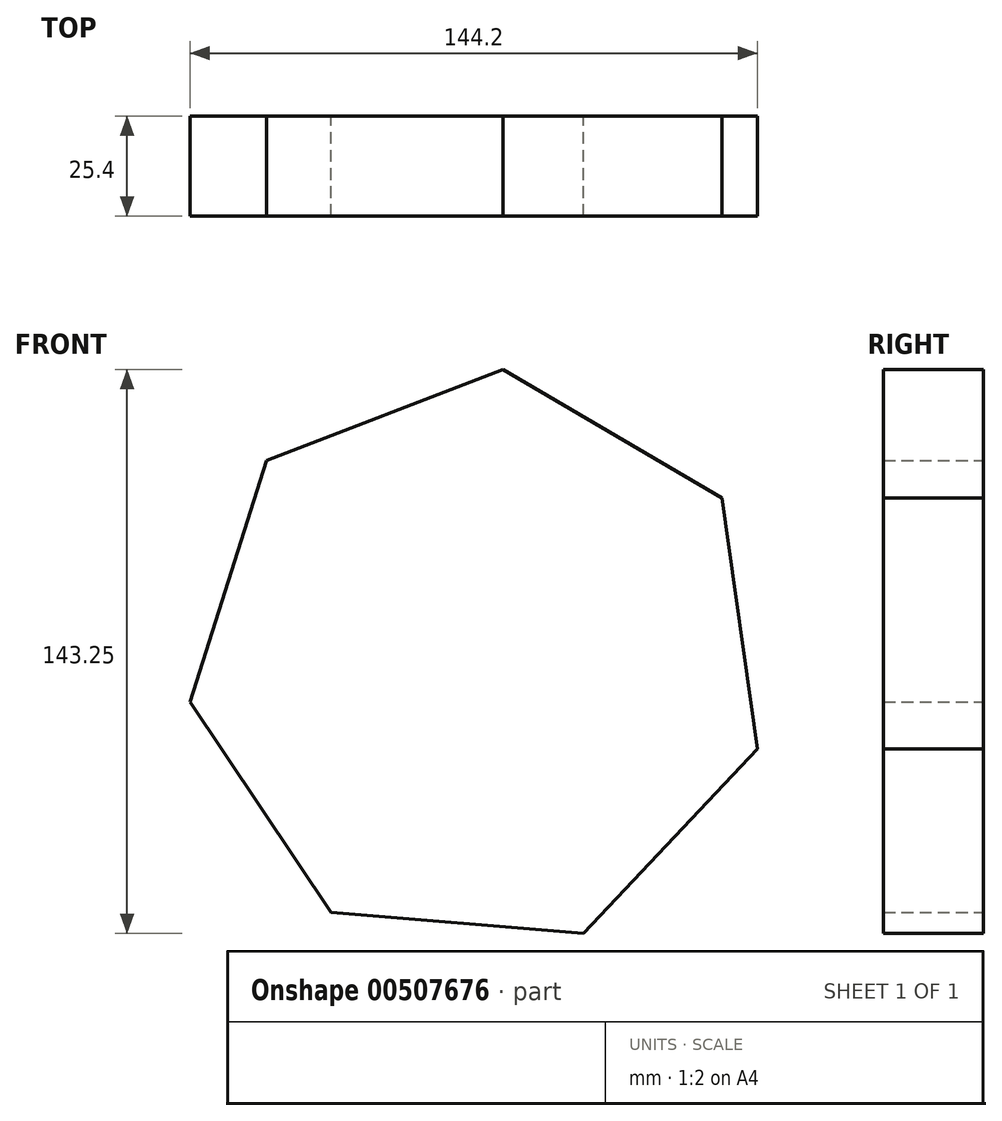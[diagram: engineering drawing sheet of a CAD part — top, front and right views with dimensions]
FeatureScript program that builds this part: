
annotation { "Feature Type Name" : "Feature", "Feature Type Description" : "" }
export const myFeature = defineFeature(function(context is Context, id is Id, definition is map)
    precondition{}
    {
        {
            var Q0;
            Q0=qCreatedBy(makeId("Front.planeOp"),FACE);
            var sketch = newSketch(context, id + "F0", { "sketchPlane" : qUnion([Q0])});
            skCircle(sketch, "E0.cCircle", {"center": v(0, 0) * mm, "radius": 74.2 * mm, "construction": true});
            skLineSegment(sketch, "E0.0", {"start": v(-37.6, -63.98) * mm, "end": v(-73.46, -10.5) * mm});
            skLineSegment(sketch, "E0.1", {"start": v(-73.46, -10.5) * mm, "end": v(-54, 50.9) * mm});
            skLineSegment(sketch, "E0.2", {"start": v(-54, 50.9) * mm, "end": v(6.12, 73.96) * mm});
            skLineSegment(sketch, "E0.3", {"start": v(6.12, 73.96) * mm, "end": v(61.64, 41.33) * mm});
            skLineSegment(sketch, "E0.4", {"start": v(61.64, 41.33) * mm, "end": v(70.74, -22.42) * mm});
            skLineSegment(sketch, "E0.5", {"start": v(70.74, -22.42) * mm, "end": v(26.58, -69.29) * mm});
            skLineSegment(sketch, "E0.6", {"start": v(26.58, -69.29) * mm, "end": v(-37.6, -63.98) * mm});
            skSolve(sketch);
        }
        {
            var Q0;
            Q0 = qSketchRegion(id + "F0", true);
            extrude(context, id + "F1", {"entities" : qUnion([Q0]), "depth" : 25.4 * mm});
        }
    });
